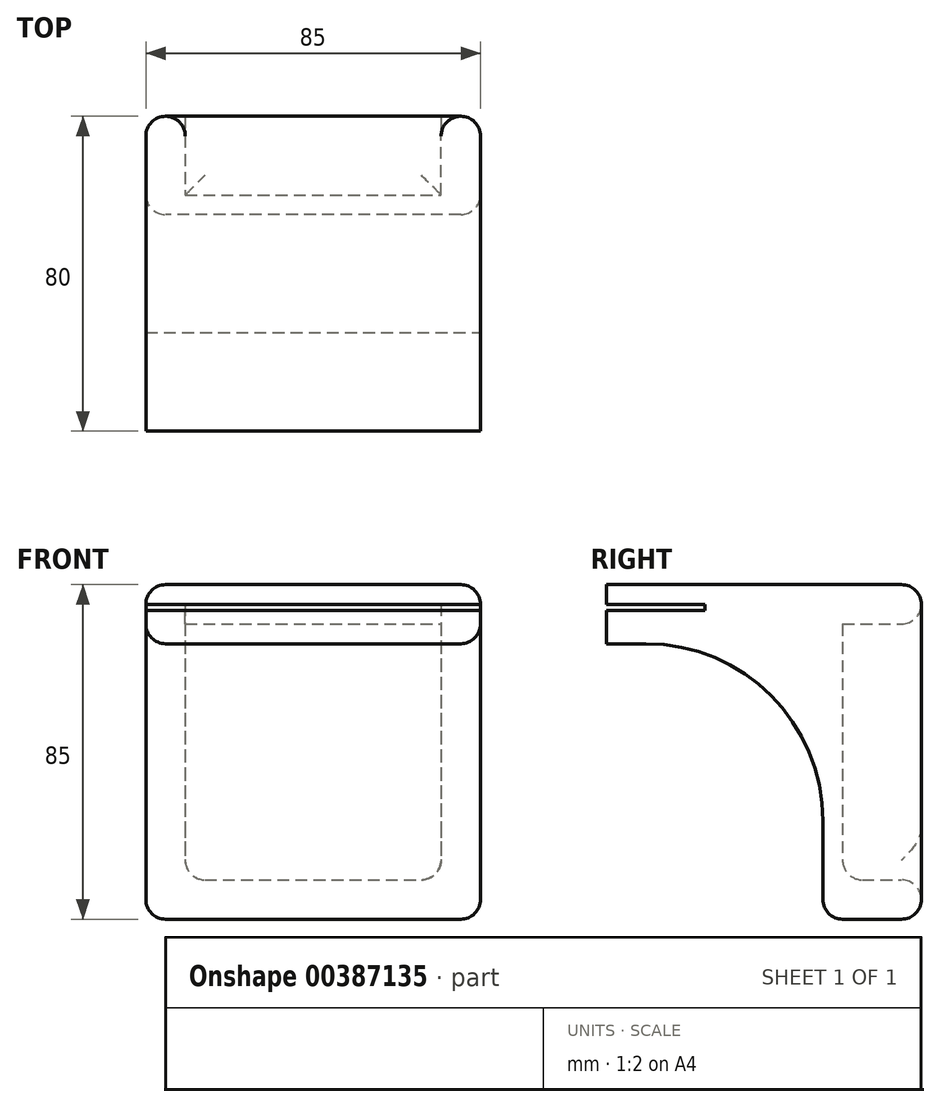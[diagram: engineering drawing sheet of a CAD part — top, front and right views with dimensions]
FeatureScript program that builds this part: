
annotation { "Feature Type Name" : "Feature", "Feature Type Description" : "" }
export const myFeature = defineFeature(function(context is Context, id is Id, definition is map)
    precondition{}
    {
        {
            var Q0;
            Q0=qCreatedBy(makeId("Top.planeOp"),FACE);
            var sketch = newSketch(context, id + "F0", { "sketchPlane" : qUnion([Q0])});
            skLineSegment(sketch, "E0.top", {"start": v(-61.82, -28) * mm, "end": v(23.18, -28) * mm});
            skLineSegment(sketch, "E0.left", {"start": v(-61.82, 57) * mm, "end": v(-61.82, -28) * mm});
            skLineSegment(sketch, "E0.right", {"start": v(23.18, 57) * mm, "end": v(23.18, -28) * mm});
            skLineSegment(sketch, "E1", {"start": v(-61.82, 57) * mm, "end": v(-51.82, 57) * mm});
            skLineSegment(sketch, "E2", {"start": v(-51.82, 57) * mm, "end": v(-51.82, 37) * mm});
            skLineSegment(sketch, "E3", {"start": v(-51.82, 37) * mm, "end": v(13.18, 37) * mm});
            skLineSegment(sketch, "E4", {"start": v(13.18, 37) * mm, "end": v(13.18, 57) * mm});
            skLineSegment(sketch, "E5", {"start": v(13.18, 57) * mm, "end": v(23.18, 57) * mm});
            skSolve(sketch);
        }
        {
            var Q0;
            Q0 = qSketchRegion(id + "F0", true);
            extrude(context, id + "F1", {"entities" : qUnion([Q0]), "depth" : 60 * mm});
        }
        {
            var Q0;
            Q0 = qSketchRegion(id + "F0", true);
            extrude(context, id + "F2", {"entities" : qUnion([Q0]), "operationType" : NewBodyOperationType.ADD, "depth" : 85 * mm});
        }
        {
            var Q0;
            Q0=makeQuery(id+"F2.opExtrude","CAP_FACE",FACE,{"disambiguationData":[OSD([sQuery(id+"F0.wireOp",EDGE,"E0.top"),sQuery(id+"F0.wireOp",EDGE,"E0.left"),sQuery(id+"F0.wireOp",EDGE,"E0.right"),sQuery(id+"F0.wireOp",EDGE,"E1"),sQuery(id+"F0.wireOp",EDGE,"E2"),sQuery(id+"F0.wireOp",EDGE,"E3"),sQuery(id+"F0.wireOp",EDGE,"E4"),sQuery(id+"F0.wireOp",EDGE,"E5")])],"isStart":false});
            var sketch = newSketch(context, id + "F3", { "sketchPlane" : qUnion([Q0])});
            skLineSegment(sketch, "E6.bottom", {"start": v(-51.82, 37) * mm, "end": v(13.18, 37) * mm});
            skLineSegment(sketch, "E6.top", {"start": v(-51.82, 57) * mm, "end": v(13.18, 57) * mm});
            skLineSegment(sketch, "E6.left", {"start": v(-51.82, 37) * mm, "end": v(-51.82, 57) * mm});
            skLineSegment(sketch, "E6.right", {"start": v(13.18, 37) * mm, "end": v(13.18, 57) * mm});
            skSolve(sketch);
        }
        {
            var Q0;
            Q0 = qSketchRegion(id + "F3", true);
            extrude(context, id + "F4", {"entities" : qUnion([Q0]), "operationType" : NewBodyOperationType.ADD, "oppositeDirection" : true, "depth" : 10 * mm});
        }
        {
            var Q0;
            Q0=makeQuery(id+"F1.opExtrude","CAP_FACE",FACE,{"disambiguationData":[OSD([sQuery(id+"F0.wireOp",EDGE,"E0.top"),sQuery(id+"F0.wireOp",EDGE,"E0.left"),sQuery(id+"F0.wireOp",EDGE,"E0.right"),sQuery(id+"F0.wireOp",EDGE,"E1"),sQuery(id+"F0.wireOp",EDGE,"E2"),sQuery(id+"F0.wireOp",EDGE,"E3"),sQuery(id+"F0.wireOp",EDGE,"E4"),sQuery(id+"F0.wireOp",EDGE,"E5")])],"isStart":true});
            var sketch = newSketch(context, id + "F5", { "sketchPlane" : qUnion([Q0])});
            skLineSegment(sketch, "E7.bottom", {"start": v(13.18, -37) * mm, "end": v(-51.82, -37) * mm});
            skLineSegment(sketch, "E7.top", {"start": v(13.18, -57) * mm, "end": v(-51.82, -57) * mm});
            skLineSegment(sketch, "E7.left", {"start": v(13.18, -37) * mm, "end": v(13.18, -57) * mm});
            skLineSegment(sketch, "E7.right", {"start": v(-51.82, -37) * mm, "end": v(-51.82, -57) * mm});
            skSolve(sketch);
        }
        {
            var Q0;
            Q0 = qSketchRegion(id + "F5", true);
            extrude(context, id + "F6", {"entities" : qUnion([Q0]), "operationType" : NewBodyOperationType.ADD, "oppositeDirection" : true, "depth" : 10 * mm});
        }
        {
            var Q0;
            Q0=makeQuery(id+"F4.boolean.opBoolean","MERGE",FACE,{"derivedFrom":[makeQuery(id+"F2.opExtrude","CAP_FACE",FACE,{"disambiguationData":[OSD([sQuery(id+"F0.wireOp",EDGE,"E0.top"),sQuery(id+"F0.wireOp",EDGE,"E0.left"),sQuery(id+"F0.wireOp",EDGE,"E0.right"),sQuery(id+"F0.wireOp",EDGE,"E1"),sQuery(id+"F0.wireOp",EDGE,"E2"),sQuery(id+"F0.wireOp",EDGE,"E3"),sQuery(id+"F0.wireOp",EDGE,"E4"),sQuery(id+"F0.wireOp",EDGE,"E5")])],"isStart":false}),makeQuery(id+"F4.opExtrude","CAP_FACE",FACE,{"disambiguationData":[OSD([sQuery(id+"F3.wireOp",EDGE,"E6.bottom"),sQuery(id+"F3.wireOp",EDGE,"E6.top"),sQuery(id+"F3.wireOp",EDGE,"E6.left"),sQuery(id+"F3.wireOp",EDGE,"E6.right")])],"isStart":true})]});
            var sketch = newSketch(context, id + "F7", { "sketchPlane" : qUnion([Q0])});
            skLineSegment(sketch, "E8.bottom", {"start": v(-61.82, -28) * mm, "end": v(23.18, -28) * mm});
            skLineSegment(sketch, "E8.top", {"start": v(-61.82, -3) * mm, "end": v(23.18, -3) * mm});
            skLineSegment(sketch, "E8.left", {"start": v(-61.82, -28) * mm, "end": v(-61.82, -3) * mm});
            skLineSegment(sketch, "E8.right", {"start": v(23.18, -28) * mm, "end": v(23.18, -3) * mm});
            skSolve(sketch);
        }
        {
            var Q0;
            Q0=makeQuery(id+"F7.imprint","IMPRINT",FACE,{"disambiguationData":[TD([[makeQuery(id+"F7.imprint","IMPRINT",EDGE,{"derivedFrom":sQuery(id+"F7.wireOp",EDGE,"E8.bottom")}),1.0]])]});
            cPlane(context, id + "F8", {"entities" : qUnion([Q0]), "cplaneType" : CPlaneType.OFFSET, "offset" : 5 * mm, "oppositeDirection" : true, "width" : 150 * mm, "height" : 150 * mm});
        }
        {
            var Q0;
            Q0=qCreatedBy(id+"F8.planeOp",FACE);
            var sketch = newSketch(context, id + "F9", { "sketchPlane" : qUnion([Q0])});
            skLineSegment(sketch, "E9.bottom", {"start": v(-61.82, -28) * mm, "end": v(23.18, -28) * mm});
            skLineSegment(sketch, "E9.top", {"start": v(-61.82, -3) * mm, "end": v(23.18, -3) * mm});
            skLineSegment(sketch, "E9.left", {"start": v(-61.82, -28) * mm, "end": v(-61.82, -3) * mm});
            skLineSegment(sketch, "E9.right", {"start": v(23.18, -28) * mm, "end": v(23.18, -3) * mm});
            skSolve(sketch);
        }
        {
            var Q0;
            Q0 = qSketchRegion(id + "F9", true);
            extrude(context, id + "F10", {"entities" : qUnion([Q0]), "operationType" : NewBodyOperationType.REMOVE, "oppositeDirection" : true, "depth" : 1.5 * mm});
        }
        {
            var Q0;
            Q0=makeQuery(id+"F6.opExtrude","CAP_FACE",FACE,{"disambiguationData":[OSD([sQuery(id+"F5.wireOp",EDGE,"E7.bottom"),sQuery(id+"F5.wireOp",EDGE,"E7.top"),sQuery(id+"F5.wireOp",EDGE,"E7.left"),sQuery(id+"F5.wireOp",EDGE,"E7.right")])],"isStart":false});
            fillet(context, id + "F11", {"entities" : qUnion([Q0]), "radius" : 5 * mm, "tangentPropagation" : true, "allowEdgeOverflow" : false});
        }
        {
            var Q0;
            Q0=makeQuery(id+"F6.boolean.opBoolean","MERGE",FACE,{"derivedFrom":[makeQuery(id+"F1.opExtrude","CAP_FACE",FACE,{"disambiguationData":[OSD([sQuery(id+"F0.wireOp",EDGE,"E0.top"),sQuery(id+"F0.wireOp",EDGE,"E0.left"),sQuery(id+"F0.wireOp",EDGE,"E0.right"),sQuery(id+"F0.wireOp",EDGE,"E1"),sQuery(id+"F0.wireOp",EDGE,"E2"),sQuery(id+"F0.wireOp",EDGE,"E3"),sQuery(id+"F0.wireOp",EDGE,"E4"),sQuery(id+"F0.wireOp",EDGE,"E5")])],"isStart":true}),makeQuery(id+"F6.opExtrude","CAP_FACE",FACE,{"disambiguationData":[OSD([sQuery(id+"F5.wireOp",EDGE,"E7.bottom"),sQuery(id+"F5.wireOp",EDGE,"E7.top"),sQuery(id+"F5.wireOp",EDGE,"E7.left"),sQuery(id+"F5.wireOp",EDGE,"E7.right")])],"isStart":true})]});
            var sketch = newSketch(context, id + "F12", { "sketchPlane" : qUnion([Q0])});
            skLineSegment(sketch, "E10.bottom", {"start": v(23.18, 28) * mm, "end": v(-61.82, 28) * mm});
            skLineSegment(sketch, "E10.top", {"start": v(23.18, -32) * mm, "end": v(-61.82, -32) * mm});
            skLineSegment(sketch, "E10.left", {"start": v(23.18, 28) * mm, "end": v(23.18, -32) * mm});
            skLineSegment(sketch, "E10.right", {"start": v(-61.82, 28) * mm, "end": v(-61.82, -32) * mm});
            skSolve(sketch);
        }
        {
            var Q0;
            Q0 = qSketchRegion(id + "F12", true);
            extrude(context, id + "F13", {"entities" : qUnion([Q0]), "operationType" : NewBodyOperationType.REMOVE, "oppositeDirection" : true, "depth" : 70 * mm});
        }
        {
            var Q0;
            Q0=makeQuery(id+"F13.boolean.opBoolean","COPY",EDGE,{"derivedFrom":makeQuery(id+"F13.opExtrude","CAP_EDGE",EDGE,{"disambiguationData":[OSD([sQuery(id+"F12.wireOp",EDGE,"E10.top")])],"isStart":false})});
            fillet(context, id + "F14", {"entities" : qUnion([Q0]), "radius" : 45 * mm, "tangentPropagation" : true, "allowEdgeOverflow" : false});
        }
        {
            var Q0;
            Q0=makeQuery(id+"F6.boolean.opBoolean","MERGE",EDGE,{"derivedFrom":[makeQuery(id+"F1.opExtrude","CAP_EDGE",EDGE,{"disambiguationData":[OSD([sQuery(id+"F0.wireOp",EDGE,"E1")])],"isStart":true}),makeQuery(id+"F1.opExtrude","CAP_EDGE",EDGE,{"disambiguationData":[OSD([sQuery(id+"F0.wireOp",EDGE,"E5")])],"isStart":true}),makeQuery(id+"F6.opExtrude","CAP_EDGE",EDGE,{"disambiguationData":[OSD([sQuery(id+"F5.wireOp",EDGE,"E7.top")])],"isStart":true})]});
            var Q1;
            {var subQ0=sQuery(id+"F0.wireOp",EDGE,"E1");var subQ1=sQuery(id+"F0.wireOp",EDGE,"E0.left");Q1=makeQuery(id+"F2.boolean.opBoolean","MERGE",EDGE,{"derivedFrom":[makeQuery(id+"F1.opExtrude","SWEPT_EDGE",EDGE,{"disambiguationData":[OSD([subQ1,subQ0])]}),makeQuery(id+"F2.opExtrude","SWEPT_EDGE",EDGE,{"disambiguationData":[OSD([subQ1,subQ0])]})]});}
            var Q2;
            {var subQ0=sQuery(id+"F0.wireOp",EDGE,"E5");var subQ1=sQuery(id+"F0.wireOp",EDGE,"E0.right");Q2=makeQuery(id+"F2.boolean.opBoolean","MERGE",EDGE,{"derivedFrom":[makeQuery(id+"F1.opExtrude","SWEPT_EDGE",EDGE,{"disambiguationData":[OSD([subQ1,subQ0])]}),makeQuery(id+"F2.opExtrude","SWEPT_EDGE",EDGE,{"disambiguationData":[OSD([subQ1,subQ0])]})]});}
            var Q3;
            Q3=makeQuery(id+"F1.opExtrude","CAP_EDGE",EDGE,{"disambiguationData":[OSD([sQuery(id+"F0.wireOp",EDGE,"E0.left")])],"isStart":true});
            var Q4;
            Q4=makeQuery(id+"F1.opExtrude","CAP_EDGE",EDGE,{"disambiguationData":[OSD([sQuery(id+"F0.wireOp",EDGE,"E0.right")])],"isStart":true});
            var Q5;
            Q5=makeQuery(id+"F13.boolean.opBoolean","COPY",EDGE,{"derivedFrom":makeQuery(id+"F13.opExtrude","CAP_EDGE",EDGE,{"disambiguationData":[OSD([sQuery(id+"F12.wireOp",EDGE,"E10.top")])],"isStart":true})});
            var Q6;
            Q6=makeQuery(id+"F13.boolean.opBoolean","COPY",EDGE,{"derivedFrom":makeQuery(id+"F13.opExtrude","CAP_EDGE",EDGE,{"disambiguationData":[OSD([sQuery(id+"F12.wireOp",EDGE,"E10.right")])],"isStart":false})});
            var Q7;
            {var subQ0=sQuery(id+"F0.wireOp",EDGE,"E0.right");Q7=makeQuery(id+"F14.opFillet","BLEND_EDGE",EDGE,{"blendedFrom":[makeQuery(id+"F13.boolean.opBoolean","COPY",EDGE,{"derivedFrom":makeQuery(id+"F13.opExtrude","CAP_EDGE",EDGE,{"disambiguationData":[OSD([sQuery(id+"F12.wireOp",EDGE,"E10.top")])],"isStart":false})}),makeQuery(id+"F2.boolean.opBoolean","MERGE",FACE,{"derivedFrom":[makeQuery(id+"F1.opExtrude","SWEPT_FACE",FACE,{"disambiguationData":[OSD([subQ0])]}),makeQuery(id+"F2.opExtrude","SWEPT_FACE",FACE,{"disambiguationData":[OSD([subQ0])]})]})],"blendedInto":[makeQuery(id+"F2.boolean.opBoolean","MERGE",FACE,{"derivedFrom":[makeQuery(id+"F1.opExtrude","SWEPT_FACE",FACE,{"disambiguationData":[OSD([subQ0])]}),makeQuery(id+"F2.opExtrude","SWEPT_FACE",FACE,{"disambiguationData":[OSD([subQ0])]})]})]});}
            var Q8;
            Q8=makeQuery(id+"F4.opExtrude","CAP_EDGE",EDGE,{"disambiguationData":[OSD([sQuery(id+"F3.wireOp",EDGE,"E6.top")])],"isStart":false});
            fillet(context, id + "F15", {"entities" : qUnion([Q0, Q1, Q2, Q3, Q4, Q5, Q6, Q7, Q8]), "radius" : 5 * mm, "tangentPropagation" : true, "allowEdgeOverflow" : false});
        }
        {
            var Q0;
            {var subQ0=sQuery(id+"F0.wireOp",EDGE,"E1");var subQ1=sQuery(id+"F0.wireOp",EDGE,"E0.left");Q0=makeQuery(id+"F2.boolean.opBoolean","MERGE",EDGE,{"derivedFrom":[makeQuery(id+"F1.opExtrude","SWEPT_EDGE",EDGE,{"disambiguationData":[OSD([subQ1,subQ0])]}),makeQuery(id+"F2.opExtrude","SWEPT_EDGE",EDGE,{"disambiguationData":[OSD([subQ1,subQ0])]})]});}
            var Q1;
            Q1=makeQuery(id+"F6.boolean.opBoolean","MERGE",FACE,{"derivedFrom":[makeQuery(id+"F1.opExtrude","CAP_FACE",FACE,{"disambiguationData":[OSD([sQuery(id+"F0.wireOp",EDGE,"E0.top"),sQuery(id+"F0.wireOp",EDGE,"E0.left"),sQuery(id+"F0.wireOp",EDGE,"E0.right"),sQuery(id+"F0.wireOp",EDGE,"E1"),sQuery(id+"F0.wireOp",EDGE,"E2"),sQuery(id+"F0.wireOp",EDGE,"E3"),sQuery(id+"F0.wireOp",EDGE,"E4"),sQuery(id+"F0.wireOp",EDGE,"E5")])],"isStart":true}),makeQuery(id+"F6.opExtrude","CAP_FACE",FACE,{"disambiguationData":[OSD([sQuery(id+"F5.wireOp",EDGE,"E7.bottom"),sQuery(id+"F5.wireOp",EDGE,"E7.top"),sQuery(id+"F5.wireOp",EDGE,"E7.left"),sQuery(id+"F5.wireOp",EDGE,"E7.right")])],"isStart":true})]});
            var Q2;
            {var subQ0=sQuery(id+"F0.wireOp",EDGE,"E5");var subQ1=sQuery(id+"F0.wireOp",EDGE,"E0.right");Q2=makeQuery(id+"F2.boolean.opBoolean","MERGE",EDGE,{"derivedFrom":[makeQuery(id+"F1.opExtrude","SWEPT_EDGE",EDGE,{"disambiguationData":[OSD([subQ1,subQ0])]}),makeQuery(id+"F2.opExtrude","SWEPT_EDGE",EDGE,{"disambiguationData":[OSD([subQ1,subQ0])]})]});}
            var Q3;
            {var subQ0=sQuery(id+"F0.wireOp",EDGE,"E0.left");Q3=makeQuery(id+"F14.opFillet","BLEND_EDGE",EDGE,{"blendedFrom":[makeQuery(id+"F13.boolean.opBoolean","COPY",EDGE,{"derivedFrom":makeQuery(id+"F13.opExtrude","CAP_EDGE",EDGE,{"disambiguationData":[OSD([sQuery(id+"F12.wireOp",EDGE,"E10.top")])],"isStart":false})}),makeQuery(id+"F2.boolean.opBoolean","MERGE",FACE,{"derivedFrom":[makeQuery(id+"F1.opExtrude","SWEPT_FACE",FACE,{"disambiguationData":[OSD([subQ0])]}),makeQuery(id+"F2.opExtrude","SWEPT_FACE",FACE,{"disambiguationData":[OSD([subQ0])]})]})],"blendedInto":[makeQuery(id+"F2.boolean.opBoolean","MERGE",FACE,{"derivedFrom":[makeQuery(id+"F1.opExtrude","SWEPT_FACE",FACE,{"disambiguationData":[OSD([subQ0])]}),makeQuery(id+"F2.opExtrude","SWEPT_FACE",FACE,{"disambiguationData":[OSD([subQ0])]})]})]});}
            var Q4;
            {var subQ0=sQuery(id+"F0.wireOp",EDGE,"E0.right");Q4=makeQuery(id+"F14.opFillet","BLEND_EDGE",EDGE,{"blendedFrom":[makeQuery(id+"F13.boolean.opBoolean","COPY",EDGE,{"derivedFrom":makeQuery(id+"F13.opExtrude","CAP_EDGE",EDGE,{"disambiguationData":[OSD([sQuery(id+"F12.wireOp",EDGE,"E10.top")])],"isStart":false})}),makeQuery(id+"F2.boolean.opBoolean","MERGE",FACE,{"derivedFrom":[makeQuery(id+"F1.opExtrude","SWEPT_FACE",FACE,{"disambiguationData":[OSD([subQ0])]}),makeQuery(id+"F2.opExtrude","SWEPT_FACE",FACE,{"disambiguationData":[OSD([subQ0])]})]})],"blendedInto":[makeQuery(id+"F2.boolean.opBoolean","MERGE",FACE,{"derivedFrom":[makeQuery(id+"F1.opExtrude","SWEPT_FACE",FACE,{"disambiguationData":[OSD([subQ0])]}),makeQuery(id+"F2.opExtrude","SWEPT_FACE",FACE,{"disambiguationData":[OSD([subQ0])]})]})]});}
            var Q5;
            Q5=makeQuery(id+"F13.boolean.opBoolean","COPY",EDGE,{"derivedFrom":makeQuery(id+"F13.opExtrude","CAP_EDGE",EDGE,{"disambiguationData":[OSD([sQuery(id+"F12.wireOp",EDGE,"E10.bottom")])],"isStart":false})});
            fillet(context, id + "F16", {"entities" : qUnion([Q0, Q1, Q2, Q3, Q4, Q5]), "radius" : 5 * mm, "tangentPropagation" : true, "allowEdgeOverflow" : false});
        }
        {
            var Q0;
            Q0=makeQuery(id+"F10.boolean.opBoolean","COPY",FACE,{"derivedFrom":makeQuery(id+"F10.opExtrude","SWEPT_FACE",FACE,{"disambiguationData":[OSD([sQuery(id+"F9.wireOp",EDGE,"E9.top")])]})});
            var sketch = newSketch(context, id + "F17", { "sketchPlane" : qUnion([Q0])});
            skLineSegment(sketch, "E11.bottom", {"start": v(23.18, 80) * mm, "end": v(-61.82, 80) * mm});
            skLineSegment(sketch, "E11.top", {"start": v(23.18, 78.5) * mm, "end": v(-61.82, 78.5) * mm});
            skLineSegment(sketch, "E11.left", {"start": v(23.18, 80) * mm, "end": v(23.18, 78.5) * mm});
            skLineSegment(sketch, "E11.right", {"start": v(-61.82, 80) * mm, "end": v(-61.82, 78.5) * mm});
            skSolve(sketch);
        }
        {
            var Q0;
            Q0 = qSketchRegion(id + "F17", true);
            extrude(context, id + "F18", {"entities" : qUnion([Q0]), "operationType" : NewBodyOperationType.REMOVE, "oppositeDirection" : true, "depth" : 5 * mm});
        }
        {
            var Q0;
            {var subQ2=sQuery(id+"F0.wireOp",EDGE,"E0.top");Q0=makeQuery(id+"F10.boolean.opBoolean","SPLIT",FACE,{"disambiguationData":[TD([makeQuery(id+"F4.opExtrude","CAP_FACE",FACE,{"disambiguationData":[OSD([sQuery(id+"F3.wireOp",EDGE,"E6.bottom"),sQuery(id+"F3.wireOp",EDGE,"E6.top"),sQuery(id+"F3.wireOp",EDGE,"E6.left"),sQuery(id+"F3.wireOp",EDGE,"E6.right")])],"isStart":true})])],"derivedFrom":makeQuery(id+"F2.boolean.opBoolean","MERGE",FACE,{"derivedFrom":[makeQuery(id+"F1.opExtrude","SWEPT_FACE",FACE,{"disambiguationData":[OSD([subQ2])]}),makeQuery(id+"F2.opExtrude","SWEPT_FACE",FACE,{"disambiguationData":[OSD([subQ2])]})]})});}
            var sketch = newSketch(context, id + "F19", { "sketchPlane" : qUnion([Q0])});
            skLineSegment(sketch, "E12.bottom", {"start": v(-61.82, 85) * mm, "end": v(23.18, 85) * mm});
            skLineSegment(sketch, "E12.top", {"start": v(-61.82, 80) * mm, "end": v(23.18, 80) * mm});
            skLineSegment(sketch, "E12.left", {"start": v(-61.82, 85) * mm, "end": v(-61.82, 80) * mm});
            skLineSegment(sketch, "E12.right", {"start": v(23.18, 85) * mm, "end": v(23.18, 80) * mm});
            skSolve(sketch);
        }
        {
            var Q0;
            Q0 = qSketchRegion(id + "F19", true);
            extrude(context, id + "F20", {"entities" : qUnion([Q0]), "operationType" : NewBodyOperationType.REMOVE, "oppositeDirection" : true, "depth" : 5 * mm});
        }
        {
            var Q0;
            {var subQ0=sQuery(id+"F0.wireOp",EDGE,"E0.left");Q0=makeQuery(id+"F2.boolean.opBoolean","MERGE",FACE,{"derivedFrom":[makeQuery(id+"F1.opExtrude","SWEPT_FACE",FACE,{"disambiguationData":[OSD([subQ0])]}),makeQuery(id+"F2.opExtrude","SWEPT_FACE",FACE,{"disambiguationData":[OSD([subQ0])]})]});}
            var sketch = newSketch(context, id + "F21", { "sketchPlane" : qUnion([Q0])});
            skLineSegment(sketch, "E13.bottom", {"start": v(28, 78.5) * mm, "end": v(23, 78.5) * mm});
            skLineSegment(sketch, "E13.top", {"start": v(28, 68.5) * mm, "end": v(23, 68.5) * mm});
            skLineSegment(sketch, "E13.left", {"start": v(28, 78.5) * mm, "end": v(28, 68.5) * mm});
            skLineSegment(sketch, "E13.right", {"start": v(23, 78.5) * mm, "end": v(23, 68.5) * mm});
            skSolve(sketch);
        }
        {
            var Q0;
            Q0 = qSketchRegion(id + "F21", true);
            extrude(context, id + "F22", {"entities" : qUnion([Q0]), "operationType" : NewBodyOperationType.REMOVE, "oppositeDirection" : true, "depth" : 85 * mm});
        }
        {
            var Q0;
            Q0=makeQuery(id+"F2.opExtrude","CAP_EDGE",EDGE,{"disambiguationData":[OSD([sQuery(id+"F0.wireOp",EDGE,"E0.right")])],"isStart":false});
            var Q1;
            {var subQ0=sQuery(id+"F12.wireOp",EDGE,"E10.bottom");Q1=makeQuery(id+"F16.opFillet","BLEND_EDGE",EDGE,{"blendedFrom":[makeQuery(id+"F13.boolean.opBoolean","COPY",EDGE,{"derivedFrom":makeQuery(id+"F13.opExtrude","CAP_EDGE",EDGE,{"disambiguationData":[OSD([subQ0])],"isStart":false})}),makeQuery(id+"F13.boolean.opBoolean","COPY",FACE,{"derivedFrom":makeQuery(id+"F13.opExtrude","CAP_FACE",FACE,{"disambiguationData":[OSD([subQ0,sQuery(id+"F12.wireOp",EDGE,"E10.top"),sQuery(id+"F12.wireOp",EDGE,"E10.left"),sQuery(id+"F12.wireOp",EDGE,"E10.right")])],"isStart":false})})],"blendedInto":[makeQuery(id+"F13.boolean.opBoolean","COPY",FACE,{"derivedFrom":makeQuery(id+"F13.opExtrude","CAP_FACE",FACE,{"disambiguationData":[OSD([subQ0,sQuery(id+"F12.wireOp",EDGE,"E10.top"),sQuery(id+"F12.wireOp",EDGE,"E10.left"),sQuery(id+"F12.wireOp",EDGE,"E10.right")])],"isStart":false})})]});}
            fillet(context, id + "F23", {"entities" : qUnion([Q0, Q1]), "radius" : 5 * mm, "tangentPropagation" : true, "allowEdgeOverflow" : false});
        }
    });
